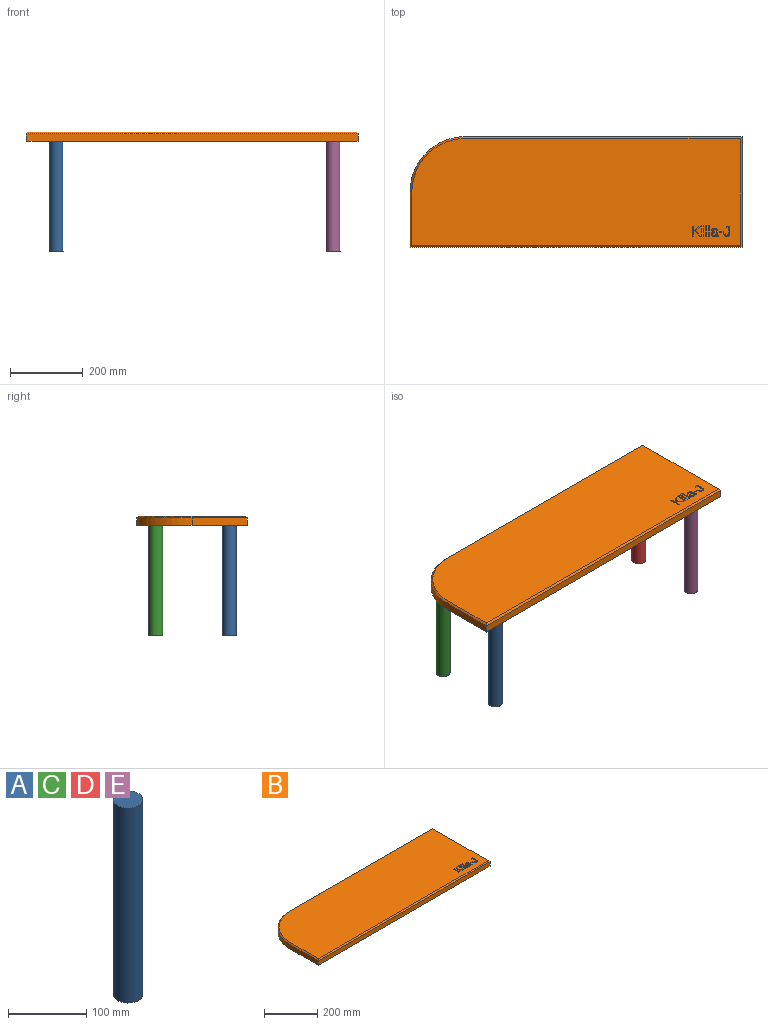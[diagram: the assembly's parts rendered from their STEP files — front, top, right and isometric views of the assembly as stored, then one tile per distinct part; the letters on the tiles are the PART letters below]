
ASSEMBLY  parts=5 mates=4
PART A: 3 faces, bbox 38.1x38.1x304.8 mm
  f0: cylinder r=19.05mm len=304.8mm, axis (0,0,1), area 36482.9mm2, adj f1,f2
  f1: plane 38.1x38.1mm, normal (0,0,-1), area 1140.1mm2, adj f0
  f2: plane 38.1x38.1mm, normal (0,0,1), area 1140.1mm2, adj f0
PART B: 101 faces, bbox 914.4x304.8x25.4 mm
  f0: plane 904.24x294.64mm, normal (0,0,1), area 260769.3mm2, adj f7,f8,f9,f10,f11,f21,f22,f23
  f1: plane 914.4x20.32mm, normal (0,-1,0), area 18580.6mm2, adj f2,f5,f6,f8
  f2: plane 304.8x20.32mm, normal (1,0,0), area 6193.5mm2, adj f1,f3,f6,f7
  f3: plane 762x20.32mm, normal (0,1,0), area 15483.8mm2, adj f2,f4,f6,f9
  f4: cylinder r=152.4mm len=152.4mm, axis (0,0,1), area 4864.4mm2, adj f3,f5,f6,f11
  f5: plane 152.4x20.32mm, normal (-1,0,0), area 3096.8mm2, adj f1,f4,f6,f10
  f6: plane 914.4x304.8mm, normal (0,0,-1), area 273724.8mm2, adj f1,f2,f3,f4,f5
  f7: plane 304.8x5.08mm, normal (0.71,0,0.71), area 2153.2mm2, adj f0,f2,f8,f9
  f8: plane 914.4x5.08mm, normal (0,-0.71,0.71), area 6532.7mm2, adj f0,f1,f7,f10
  f9: plane 762x5.08mm, normal (0,0.71,0.71), area 5456.1mm2, adj f0,f3,f7,f11
  f10: plane 152.4x5.08mm, normal (-0.71,0,0.71), area 1076.6mm2, adj f0,f5,f8,f11
  f11: cone r=147.32mm half-angle=45deg, axis (0,0,-1), area 1691.2mm2, adj f0,f4,f9,f10
  f12: extruded ~6.35x3.47mm, area 23mm2, adj f13,f46,f47,f100
  f13: extruded ~6.35x2.67mm, area 18.5mm2, adj f12,f14,f47,f100
  f14: extruded ~6.35x2.68mm, area 18.5mm2, adj f13,f15,f47,f100
  f15: extruded ~6.35x2.58mm, area 17.2mm2, adj f14,f16,f47,f100
  f16: extruded ~6.35x1.98mm, area 15.8mm2, adj f15,f17,f47,f100
  f17: extruded ~6.35x3.79mm, area 24.4mm2, adj f16,f18,f47,f100
  f18: plane 6.35x3.88mm, normal (-0.02,1,0), area 24.7mm2, adj f17,f19,f47,f100
  f19: plane 6.35x1.75mm, normal (1,0,0), area 11.1mm2, adj f18,f20,f47,f100
  f20: extruded ~6.35x3.18mm, area 21.2mm2, adj f19,f46,f47,f100
  f21: extruded ~6.35x4.83mm, area 33.4mm2, adj f0,f22,f45,f47
  f22: extruded ~6.35x4.38mm, area 28.9mm2, adj f0,f21,f23,f47
  f23: extruded ~6.35x3.46mm, area 30.1mm2, adj f0,f22,f24,f47
  f24: plane 6.35x0.11mm, normal (0,1,0), area 0.7mm2, adj f0,f23,f25,f47
  f25: extruded ~6.35x3.24mm, area 21.9mm2, adj f0,f24,f26,f47
  f26: extruded ~6.35x2.86mm, area 19.9mm2, adj f0,f25,f27,f47
  f27: extruded ~6.35x2.73mm, area 17.5mm2, adj f0,f26,f28,f47
  f28: plane 6.35x2.21mm, normal (-1,0,0), area 14mm2, adj f0,f27,f29,f47
  f29: extruded ~6.35x1.16mm, area 7.4mm2, adj f0,f28,f30,f47
  f30: extruded ~6.35x1.58mm, area 11.8mm2, adj f0,f29,f31,f47
  f31: extruded ~6.35x2.37mm, area 15.4mm2, adj f0,f30,f32,f47
  f32: plane 9.17x6.35mm, normal (-1,0,0), area 58.3mm2, adj f0,f31,f33,f47
  f33: extruded ~6.35x5.33mm, area 37.3mm2, adj f0,f32,f34,f47
  f34: extruded ~6.35x6.05mm, area 41.1mm2, adj f0,f33,f35,f47
  f35: extruded ~8.54x6.35mm, area 72.4mm2, adj f0,f34,f36,f47
  f36: plane 6.35x3.7mm, normal (0.09,1,0), area 23.6mm2, adj f0,f35,f37,f47
  f37: extruded ~6.35x2.58mm, area 18.9mm2, adj f0,f36,f38,f47
  f38: extruded ~6.35x3.47mm, area 23mm2, adj f0,f37,f39,f47
  f39: extruded ~6.35x3.47mm, area 23.8mm2, adj f0,f38,f40,f47
  f40: extruded ~6.35x3.72mm, area 25.2mm2, adj f0,f39,f41,f47
  f41: plane 6.35x1.16mm, normal (1,0,0), area 7.4mm2, adj f0,f40,f42,f47
  f42: plane 6.35x4.79mm, normal (0.02,-1,0), area 30.4mm2, adj f0,f41,f43,f47
  f43: extruded ~7.02x6.35mm, area 46.9mm2, adj f0,f42,f44,f47
  f44: extruded ~6.35x5.08mm, area 36.4mm2, adj f0,f43,f45,f47
  f45: extruded ~6.35x4.65mm, area 32mm2, adj f0,f21,f44,f47
  f46: extruded ~6.35x2.43mm, area 21.9mm2, adj f12,f20,f47,f100
  f47: plane 22.1x20.71mm, normal (0,0,1), area 207.4mm2, adj f12,f13,f14,f15,f16,f17,f18,f19
  f48: extruded ~8.37x7.29mm, area 78mm2, adj f0,f49,f60,f61
  f49: extruded ~6.35x5.99mm, area 42mm2, adj f0,f48,f50,f61
  f50: extruded ~6.35x6.35mm, area 43.7mm2, adj f0,f49,f51,f61
  f51: plane 19.47x6.35mm, normal (-1,0,0), area 123.6mm2, adj f0,f50,f52,f61
  f52: plane 9.08x6.35mm, normal (0,-1,0), area 57.7mm2, adj f0,f51,f53,f61
  f53: plane 6.35x3.07mm, normal (1,0,0), area 19.5mm2, adj f0,f52,f54,f61
  f54: plane 6.35x5.34mm, normal (0,1,0), area 33.9mm2, adj f0,f53,f55,f61
  f55: plane 16.48x6.35mm, normal (1,0,0), area 104.7mm2, adj f0,f54,f56,f61
  f56: extruded ~6.35x4.12mm, area 27.8mm2, adj f0,f55,f57,f61
  f57: extruded ~6.35x3.23mm, area 23.2mm2, adj f0,f56,f58,f61
  f58: extruded ~6.35x3.11mm, area 22mm2, adj f0,f57,f59,f61
  f59: extruded ~6.35x3.57mm, area 25.2mm2, adj f0,f58,f60,f61
  f60: plane 6.35x3.68mm, normal (0.16,-0.99,0), area 23.7mm2, adj f0,f48,f59,f61
  f61: plane 28.14x16.54mm, normal (0,0,1), area 160.7mm2, adj f48,f49,f50,f51,f52,f53,f54,f55
  f62: plane 6.35x3.15mm, normal (1,0,0), area 20mm2, adj f0,f63,f65,f66
  f63: plane 9.85x6.35mm, normal (0,1,0), area 62.5mm2, adj f0,f62,f64,f66
  f64: plane 6.35x3.15mm, normal (-1,0,0), area 20mm2, adj f0,f63,f65,f66
  f65: plane 9.85x6.35mm, normal (0,-1,0), area 62.5mm2, adj f0,f62,f64,f66
  f66: plane 9.85x3.15mm, normal (0,0,1), area 31mm2, adj f62,f63,f64,f65
  f67: plane 29.22x6.35mm, normal (1,0,0), area 185.6mm2, adj f0,f68,f70,f71
  f68: plane 6.35x3.55mm, normal (0,1,0), area 22.5mm2, adj f0,f67,f69,f71
  f69: plane 29.22x6.35mm, normal (-1,0,0), area 185.6mm2, adj f0,f68,f70,f71
  f70: plane 6.35x3.55mm, normal (0,-1,0), area 22.5mm2, adj f0,f67,f69,f71
  f71: plane 29.22x3.55mm, normal (0,0,1), area 103.7mm2, adj f67,f68,f69,f70
  f72: plane 29.22x6.35mm, normal (1,0,0), area 185.6mm2, adj f0,f73,f75,f76
  f73: plane 6.35x3.55mm, normal (0,1,0), area 22.5mm2, adj f0,f72,f74,f76
  f74: plane 29.22x6.35mm, normal (-1,0,0), area 185.6mm2, adj f0,f73,f75,f76
  f75: plane 6.35x3.55mm, normal (0,-1,0), area 22.5mm2, adj f0,f72,f74,f76
  f76: plane 29.22x3.55mm, normal (0,0,1), area 103.7mm2, adj f72,f73,f74,f75
  f77: plane 21.3x6.35mm, normal (1,0,0), area 135.3mm2, adj f0,f78,f80,f81
  f78: plane 6.35x3.55mm, normal (0,1,0), area 22.5mm2, adj f0,f77,f79,f81
  f79: plane 21.3x6.35mm, normal (-1,0,0), area 135.3mm2, adj f0,f78,f80,f81
  f80: plane 6.35x3.55mm, normal (0,-1,0), area 22.5mm2, adj f0,f77,f79,f81
  f81: plane 21.3x3.55mm, normal (0,0,1), area 75.6mm2, adj f77,f78,f79,f80
  f82: plane 6.35x3.39mm, normal (1,0,0), area 21.5mm2, adj f0,f83,f85,f86
  f83: plane 6.35x3.55mm, normal (0,1,0), area 22.5mm2, adj f0,f82,f84,f86
  f84: plane 6.35x3.39mm, normal (-1,0,0), area 21.5mm2, adj f0,f83,f85,f86
  f85: plane 6.35x3.55mm, normal (0,-1,0), area 22.5mm2, adj f0,f82,f84,f86
  f86: plane 3.55x3.39mm, normal (0,0,1), area 12mm2, adj f82,f83,f84,f85
  f87: plane 13.39x11.08mm, normal (0.77,0.64,0), area 110.4mm2, adj f0,f88,f98,f99
  f88: plane 6.35x4.67mm, normal (0,1,0), area 29.6mm2, adj f0,f87,f89,f99
  f89: plane 15.7x13.39mm, normal (-0.76,-0.65,0), area 131mm2, adj f0,f88,f90,f99
  f90: plane 12.05x11.81mm, normal (-0.71,0.7,0), area 107.1mm2, adj f0,f89,f91,f99
  f91: plane 6.35x4.43mm, normal (0,-1,0), area 28.1mm2, adj f0,f90,f92,f99
  f92: plane 13.9x13.37mm, normal (0.72,-0.69,0), area 122.5mm2, adj f0,f91,f93,f99
  f93: plane 13.9x6.35mm, normal (-1,0,0), area 88.3mm2, adj f0,f92,f94,f99
  f94: plane 6.35x3.76mm, normal (0,-1,0), area 23.9mm2, adj f0,f93,f95,f99
  f95: plane 27.74x6.35mm, normal (1,0,0), area 176.2mm2, adj f0,f94,f96,f99
  f96: plane 6.35x3.76mm, normal (0,1,0), area 23.9mm2, adj f0,f95,f97,f99
  f97: plane 10.64x6.35mm, normal (-1,0,0), area 67.5mm2, adj f0,f96,f98,f99
  f98: plane 6.35x3.62mm, normal (-0.61,0.8,0), area 28.9mm2, adj f0,f87,f97,f99
  f99: plane 27.74x23.14mm, normal (0,0,1), area 236mm2, adj f87,f88,f89,f90,f91,f92,f93,f94
  f100: plane 10.34x8.25mm, normal (0,0,1), area 68.4mm2, adj f12,f13,f14,f15,f16,f17,f18,f19
PART C: same geometry as A
PART D: same geometry as A
PART E: same geometry as A
PLACE A t=(7.71,-27.56,0)mm
PLACE B at identity fixed
PLACE C t=(7.71,175.64,0)mm
PLACE D t=(769.71,175.64,0)mm
PLACE E t=(769.71,-27.56,0)mm
MATE fastened A.f0 <-> B.f6  axis (0,0,1) through (83.91,48.64,-25.4)mm
MATE fastened D.f0 <-> B.f6  axis (0,0,1) through (845.91,251.84,-25.4)mm
MATE fastened C.f0 <-> B.f6  axis (0,0,1) through (83.91,251.84,-25.4)mm
MATE fastened E.f0 <-> B.f6  axis (0,0,1) through (845.91,48.64,-25.4)mm
